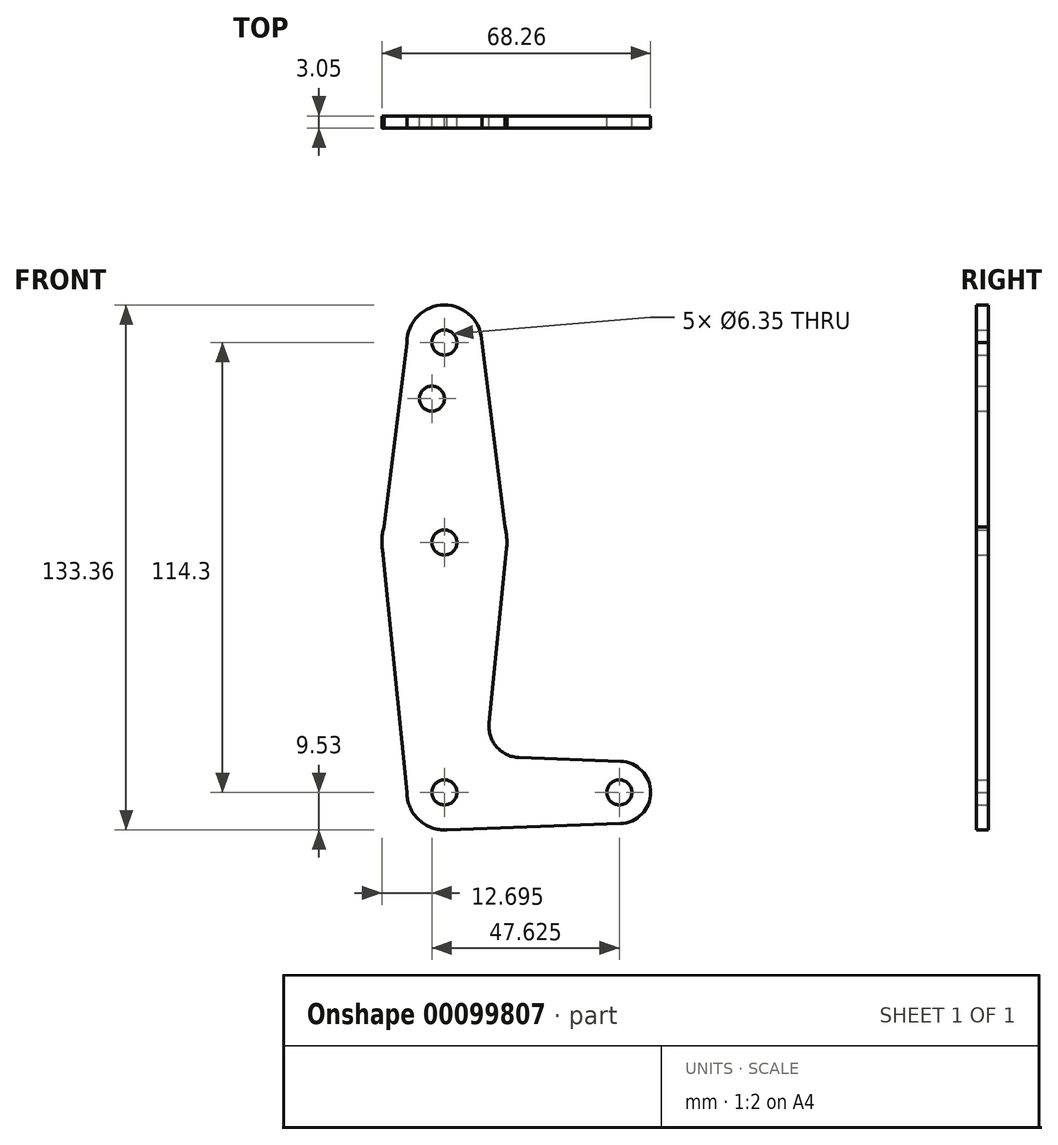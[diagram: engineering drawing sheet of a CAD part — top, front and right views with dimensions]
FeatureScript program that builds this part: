
annotation { "Feature Type Name" : "Feature", "Feature Type Description" : "" }
export const myFeature = defineFeature(function(context is Context, id is Id, definition is map)
    precondition{}
    {
        {
            var Q0;
            Q0=qCreatedBy(makeId("Front.planeOp"),FACE);
            var sketch = newSketch(context, id + "F0", { "sketchPlane" : qUnion([Q0])});
            skLineSegment(sketch, "E0", {"start": v(0, 0) * mm, "end": v(44.45, 0) * mm, "construction": true});
            skLineSegment(sketch, "E1", {"start": v(44.45, 0) * mm, "end": v(0, 0) * mm, "construction": true});
            skCircle(sketch, "E2", {"center": v(0, 0) * mm, "radius": 9.53 * mm});
            skCircle(sketch, "E3", {"center": v(44.45, 0) * mm, "radius": 7.94 * mm});
            skLineSegment(sketch, "E4", {"start": v(0, 0) * mm, "end": v(0, 114.3) * mm, "construction": true});
            skCircle(sketch, "E5", {"center": v(0, 114.3) * mm, "radius": 9.53 * mm});
            skCircle(sketch, "E6", {"center": v(0, 63.5) * mm, "radius": 15.88 * mm});
            skLineSegment(sketch, "E7", {"start": v(9.53, 114.3) * mm, "end": v(15.88, 63.5) * mm});
            skLineSegment(sketch, "E8", {"start": v(0, -9.53) * mm, "end": v(44.73, -7.93) * mm});
            skLineSegment(sketch, "E9", {"start": v(-9.52, 0) * mm, "end": v(-15.88, 63.5) * mm});
            skLineSegment(sketch, "E10", {"start": v(-15.88, 63.5) * mm, "end": v(-9.53, 114.3) * mm});
            skCircle(sketch, "E11", {"center": v(0, 114.3) * mm, "radius": 3.18 * mm});
            skCircle(sketch, "E12", {"center": v(0, 63.5) * mm, "radius": 3.18 * mm});
            skCircle(sketch, "E13", {"center": v(0, 0) * mm, "radius": 3.18 * mm});
            skCircle(sketch, "E14", {"center": v(44.45, 0) * mm, "radius": 3.18 * mm});
            skLineSegment(sketch, "E15", {"start": v(44.73, 7.93) * mm, "end": v(18.97, 8.85) * mm});
            skLineSegment(sketch, "E16", {"start": v(15.8, 61.91) * mm, "end": v(11.34, 17.6) * mm});
            skArc(sketch, "E17.filletArc", {"start": v(11.34, 17.6) * mm, "mid": v(13.26, 11.57) * mm, "end": v(18.97, 8.85) * mm});
            skCircle(sketch, "E18", {"center": v(-3.18, 100.03) * mm, "radius": 3.18 * mm});
            skSolve(sketch);
        }
        {
            var Q0;
            Q0 = qSketchRegion(id + "F0", true);
            extrude(context, id + "F1", {"entities" : qUnion([Q0]), "depth" : 3.05 * mm});
        }
    });
